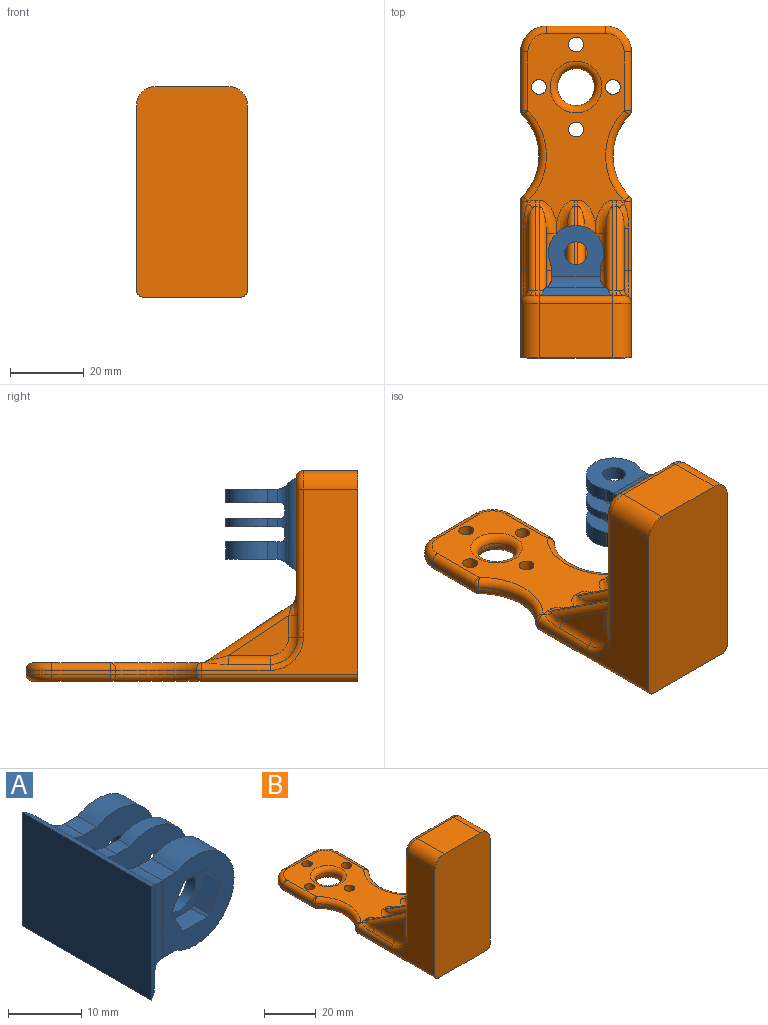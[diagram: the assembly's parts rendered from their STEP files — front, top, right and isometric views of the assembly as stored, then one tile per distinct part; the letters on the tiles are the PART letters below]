
ASSEMBLY  parts=2 mates=1
PART A: 42 faces, bbox 19x25x19 mm
  f0: plane 15x13.87mm, normal (0,-1,0), area 116.1mm2, adj f2,f6,f11,f16,f17,f18,f21,f29
  f1: cylinder r=3.7mm len=21.8mm, axis (0,-1,0), area 48.8mm2, adj f2,f3,f9,f12,f13,f14,f15,f21
  f2: plane 4.75x2.63mm, normal (0,0,-1), area 12.5mm2, adj f0,f1,f6,f27
  f3: plane 2.63x2.3mm, normal (0,0,-1), area 6mm2, adj f1,f10,f15,f28
  f4: plane 3.75x2.63mm, normal (0,0,1), area 9.8mm2, adj f7,f13,f19,f22
  f5: plane 2.63x2.3mm, normal (0,0,1), area 6mm2, adj f10,f15,f22,f28
  f6: cylinder r=7.5mm len=15mm, axis (0,1,0), area 149.1mm2, adj f0,f2,f11,f27
  f7: cylinder r=7.5mm len=15mm, axis (0,1,0), area 117.7mm2, adj f4,f9,f13,f19
  f8: plane 9.67x8.25mm, normal (0,-1,0), area 29.9mm2, adj f16,f17,f18,f26,f29,f30,f31,f32
  f9: plane 3.75x2.63mm, normal (0,0,-1), area 9.8mm2, adj f1,f7,f13,f19
  f10: cylinder r=7.5mm len=15mm, axis (0,1,0), area 72.2mm2, adj f3,f5,f15,f28
  f11: plane 4.75x2.63mm, normal (0,0,1), area 12.5mm2, adj f0,f6,f22,f27
  f12: plane 14.35x2.1mm, normal (1,0,0), area 30.1mm2, adj f1,f22,f38,f40
  f13: plane 15x15mm, normal (0,-1,0), area 160.9mm2, adj f1,f4,f7,f9,f22,f24,f40
  f14: plane 14.35x2.1mm, normal (1,0,0), area 30.1mm2, adj f1,f22,f39,f41
  f15: plane 15x15mm, normal (0,-1,0), area 160.9mm2, adj f1,f3,f5,f10,f22,f25,f41
  f16: plane 4.62x3mm, normal (0,0,1), area 13.9mm2, adj f0,f8,f18,f29
  f17: plane 4x3mm, normal (0.87,0,-0.5), area 13.9mm2, adj f0,f8,f18,f32
  f18: plane 4x3mm, normal (0.87,0,0.5), area 13.9mm2, adj f0,f8,f16,f17
  f19: plane 15x13.87mm, normal (0,1,0), area 146mm2, adj f4,f7,f9,f23,f24
  f20: plane 25x19mm, normal (-1,0,0), area 475mm2, adj f34,f35,f36,f37
  f21: cylinder r=3.7mm len=15.8mm, axis (0,0,1), area 46.5mm2, adj f0,f1,f22,f35
  f22: cylinder r=3.7mm len=21.8mm, axis (0,-1,0), area 48.8mm2, adj f4,f5,f11,f12,f13,f14,f15,f21
  f23: cylinder r=3.7mm len=15.8mm, axis (0,0,1), area 46.5mm2, adj f1,f19,f22,f36
  f24: cylinder r=3.1mm len=6.2mm, axis (0,-1,0), area 73mm2, adj f13,f19
  f25: cylinder r=3.1mm len=6.2mm, axis (0,-1,0), area 44.8mm2, adj f15,f28
  f26: cylinder r=3.1mm len=6.2mm, axis (0,-1,0), area 34.1mm2, adj f8,f27
  f27: plane 15x15mm, normal (0,1,0), area 160.9mm2, adj f1,f2,f6,f11,f22,f26,f39
  f28: plane 15x15mm, normal (0,1,0), area 160.9mm2, adj f1,f3,f5,f10,f22,f25,f38
  f29: plane 3x0.43mm, normal (-0.5,0,0.87), area 1.5mm2, adj f0,f8,f16,f30
  f30: plane 4x3mm, normal (-0.87,0,0.5), area 13.9mm2, adj f0,f8,f29,f31
  f31: plane 4x3mm, normal (-0.87,0,-0.5), area 13.9mm2, adj f0,f8,f30,f33
  f32: plane 3x0.43mm, normal (0.5,0,-0.87), area 1.5mm2, adj f0,f8,f17,f33
  f33: plane 4.62x3mm, normal (0,0,-1), area 13.9mm2, adj f0,f8,f31,f32
  f34: cylinder r=5mm len=25mm, axis (0,1,0), area 65.7mm2, adj f20,f22,f35,f36
  f35: cylinder r=5mm len=19mm, axis (0,0,-1), area 49mm2, adj f20,f21,f34,f37
  f36: cylinder r=5mm len=19mm, axis (0,0,-1), area 49mm2, adj f20,f23,f34,f37
  f37: cylinder r=5mm len=25mm, axis (0,1,0), area 65.7mm2, adj f1,f20,f35,f36
  f38: cylinder r=1mm len=14.35mm, axis (0,0,-1), area 21.9mm2, adj f1,f12,f22,f28
  f39: cylinder r=1mm len=14.35mm, axis (0,0,-1), area 21.9mm2, adj f1,f14,f22,f27
  f40: cylinder r=1mm len=14.35mm, axis (0,0,-1), area 21.9mm2, adj f1,f12,f13,f22
  f41: cylinder r=1mm len=14.35mm, axis (0,0,-1), area 21.9mm2, adj f1,f14,f15,f22
PART B: 121 faces, bbox 32.5x90.9x57.9 mm
  f0: plane 35.95x26mm, normal (0,1,0), area 845.2mm2, adj f27,f28,f29,f66,f68,f70,f72,f75
  f1: plane 16.36x10.84mm, normal (-1,0,0), area 83.3mm2, adj f63,f67,f69,f71
  f2: plane 16.36x10.84mm, normal (1,0,0), area 83.3mm2, adj f64,f90,f94,f98
  f3: plane 51.85x26.53mm, normal (0,0,1), area 821.4mm2, adj f14,f15,f16,f17,f32,f33,f34,f35
  f4: plane 21.5x14.5mm, normal (-1,0,0), area 171.8mm2, adj f6,f7,f10,f23,f24
  f5: plane 21.5x14.5mm, normal (1,0,0), area 171.8mm2, adj f6,f7,f10,f23,f24
  f6: plane 21.5x7.5mm, normal (0,0,-1), area 161.3mm2, adj f4,f5,f7,f23
  f7: plane 21.5x14.5mm, normal (0,-1,0), area 311.7mm2, adj f4,f5,f6,f24
  f8: plane 15.86x1mm, normal (1,0,0), area 15.9mm2, adj f25,f36,f45,f109
  f9: plane 15.86x1mm, normal (-1,0,0), area 15.9mm2, adj f26,f37,f46,f106
  f10: plane 87.75x26mm, normal (0,0,-1), area 1586mm2, adj f4,f5,f14,f15,f16,f17,f22,f23
  f11: plane 50x42.36mm, normal (1,0,0), area 782.5mm2, adj f22,f28,f30,f32,f41,f112,f117
  f12: plane 16x1mm, normal (0,1,0), area 16mm2, adj f25,f26,f40,f49
  f13: cylinder r=5mm len=10mm, axis (0,0,-1), area 31.4mm2, adj f50,f51
  f14: cylinder r=2mm len=5mm, axis (0,0,-1), area 62.8mm2, adj f3,f10
  f15: cylinder r=2mm len=5mm, axis (0,0,-1), area 62.8mm2, adj f3,f10
  f16: cylinder r=2mm len=5mm, axis (0,0,-1), area 62.8mm2, adj f3,f10
  f17: cylinder r=2mm len=5mm, axis (0,0,-1), area 62.8mm2, adj f3,f10
  f18: plane 50x42.36mm, normal (-1,0,0), area 782.5mm2, adj f22,f29,f31,f33,f42,f115,f119
  f19: cylinder r=15.54mm len=21.73mm, axis (0,0,1), area 24.1mm2, adj f34,f43,f109,f112
  f20: cylinder r=15.54mm len=21.73mm, axis (0,0,1), area 24.1mm2, adj f35,f44,f106,f115
  f21: plane 20x14.75mm, normal (0,0,1), area 295mm2, adj f22,f27,f117,f119
  f22: plane 57x30mm, normal (0,-1,0), area 1697.6mm2, adj f10,f11,f18,f21,f41,f42,f117,f119
  f23: plane 21.5x21.5mm, normal (0,1,0), area 462.2mm2, adj f4,f5,f6,f10
  f24: cylinder r=7mm len=21.5mm, axis (1,0,0), area 236.4mm2, adj f4,f5,f7,f10
  f25: cylinder r=7mm len=7mm, axis (0,0,-1), area 11mm2, adj f8,f12,f38,f47
  f26: cylinder r=7mm len=7mm, axis (0,0,1), area 11mm2, adj f9,f12,f39,f48
  f27: cylinder r=2mm len=20mm, axis (1,0,0), area 62.8mm2, adj f0,f21,f118,f120
  f28: cylinder r=2mm len=40mm, axis (0,0,1), area 115mm2, adj f0,f11,f30,f85,f90,f118
  f29: cylinder r=2mm len=40mm, axis (0,0,-1), area 115mm2, adj f0,f18,f31,f65,f67,f120
  f30: torus R=9mm, axis (-1,0,0), area 23.7mm2, adj f11,f28,f32,f94
  f31: torus R=9mm, axis (-1,0,0), area 23.7mm2, adj f18,f29,f33,f69
  f32: cylinder r=2mm len=18.61mm, axis (0,-1,0), area 37.6mm2, adj f3,f11,f30,f98,f101,f111
  f33: cylinder r=2mm len=18.61mm, axis (0,1,0), area 37.6mm2, adj f3,f18,f31,f71,f74,f114
  f34: torus R=17.54mm, axis (0,0,1), area 79.1mm2, adj f3,f19,f108,f111
  f35: torus R=17.54mm, axis (0,0,1), area 79.1mm2, adj f3,f20,f105,f114
  f36: cylinder r=2mm len=15.86mm, axis (0,-1,0), area 49.8mm2, adj f3,f8,f38,f108
  f37: cylinder r=2mm len=15.86mm, axis (0,1,0), area 49.8mm2, adj f3,f9,f39,f105
  f38: torus R=5mm, axis (0,0,1), area 31mm2, adj f3,f25,f36,f40
  f39: torus R=5mm, axis (0,0,1), area 31mm2, adj f3,f26,f37,f40
  f40: cylinder r=2mm len=16mm, axis (1,0,0), area 50.3mm2, adj f3,f12,f38,f39
  f41: cylinder r=2mm len=42.36mm, axis (0,1,0), area 133.1mm2, adj f10,f11,f22,f113
  f42: cylinder r=2mm len=42.36mm, axis (0,-1,0), area 133.1mm2, adj f10,f18,f22,f116
  f43: torus R=17.54mm, axis (0,0,1), area 79.1mm2, adj f10,f19,f110,f113
  f44: torus R=17.54mm, axis (0,0,1), area 79.1mm2, adj f10,f20,f107,f116
  f45: cylinder r=2mm len=15.86mm, axis (0,1,0), area 49.8mm2, adj f8,f10,f47,f110
  f46: cylinder r=2mm len=15.86mm, axis (0,-1,0), area 49.8mm2, adj f9,f10,f48,f107
  f47: torus R=5mm, axis (0,0,1), area 31mm2, adj f10,f25,f45,f49
  f48: torus R=5mm, axis (0,0,1), area 31mm2, adj f10,f26,f46,f49
  f49: cylinder r=2mm len=16mm, axis (-1,0,0), area 50.3mm2, adj f10,f12,f47,f48
  f50: torus R=7mm, axis (0,0,1), area 113mm2, adj f10,f13
  f51: torus R=7mm, axis (0,0,1), area 113mm2, adj f3,f13
  f52: plane 13.85x9.18mm, normal (1,0,0), area 60.1mm2, adj f59,f73,f77,f83
  f53: plane 13.85x9.18mm, normal (-1,0,0), area 60.1mm2, adj f60,f76,f82,f88
  f54: plane 13.85x9.18mm, normal (1,0,0), area 60.1mm2, adj f61,f87,f92,f96
  f55: plane 13.85x9.18mm, normal (-1,0,0), area 60.1mm2, adj f62,f91,f95,f99
  f56: plane 22.9x15.18mm, normal (0,0.55,0.83), area 27.5mm2, adj f62,f64,f80,f104
  f57: plane 22.9x15.18mm, normal (0,0.55,0.83), area 27.5mm2, adj f60,f61,f75,f97
  f58: plane 22.9x15.18mm, normal (0,0.55,0.83), area 27.5mm2, adj f59,f63,f68,f84
  f59: cylinder r=2mm len=24.01mm, axis (0,-0.83,0.55), area 69.3mm2, adj f52,f58,f70,f89
  f60: cylinder r=2mm len=24.01mm, axis (0,0.83,-0.55), area 69.3mm2, adj f53,f57,f72,f93
  f61: cylinder r=2mm len=24.01mm, axis (0,-0.83,0.55), area 69.3mm2, adj f54,f57,f81,f100
  f62: cylinder r=2mm len=24.01mm, axis (0,0.83,-0.55), area 69.3mm2, adj f55,f56,f86,f102
  f63: cylinder r=2mm len=24.01mm, axis (0,-0.83,0.55), area 75.8mm2, adj f1,f58,f65,f66,f74,f78
  f64: cylinder r=2mm len=24.01mm, axis (0,0.83,-0.55), area 75.8mm2, adj f2,f56,f79,f85,f101,f103
  f65: bspline ~5.65x2.62mm, area 9.9mm2, adj f29,f63,f66,f67
  f66: bspline ~2.79x2mm, area 4.3mm2, adj f0,f63,f65,f68
  f67: cylinder r=3mm len=5.84mm, axis (0,0,-1), area 16.2mm2, adj f1,f29,f65,f69
  f68: cylinder r=3mm len=2.5mm, axis (1,0,0), area 3mm2, adj f0,f58,f66,f70
  f69: torus R=5mm, axis (-1,0,0), area 27.5mm2, adj f1,f31,f67,f71
  f70: bspline ~6x5mm, area 22.5mm2, adj f0,f59,f68,f72,f73
  f71: cylinder r=3mm len=11.36mm, axis (0,1,0), area 31.6mm2, adj f1,f33,f69,f74
  f72: bspline ~6x5mm, area 22.5mm2, adj f0,f60,f70,f75,f76
  f73: cylinder r=3mm len=5.18mm, axis (0,0,-1), area 23.1mm2, adj f52,f70,f76,f77
  f74: bspline ~9.27x3.03mm, area 13.1mm2, adj f33,f63,f71,f78
  f75: cylinder r=3mm len=2.5mm, axis (1,0,0), area 3mm2, adj f0,f57,f72,f81
  f76: cylinder r=3mm len=5.18mm, axis (0,0,1), area 23.1mm2, adj f53,f72,f73,f82
  f77: torus R=4mm, axis (-1,0,0), area 41mm2, adj f52,f73,f82,f83
  f78: bspline ~2.27x2mm, area 3mm2, adj f3,f63,f74,f84
  f79: bspline ~2.79x2mm, area 4.3mm2, adj f0,f64,f80,f85
  f80: cylinder r=3mm len=2.5mm, axis (1,0,0), area 3mm2, adj f0,f56,f79,f86
  f81: bspline ~7.04x5mm, area 22.5mm2, adj f0,f61,f75,f86,f87
  f82: torus R=4mm, axis (-1,0,0), area 41mm2, adj f53,f76,f77,f88
  f83: cylinder r=3mm len=9.85mm, axis (0,1,0), area 44mm2, adj f52,f77,f88,f89
  f84: cylinder r=3mm len=1.66mm, axis (1,0,0), area 1.8mm2, adj f3,f58,f78,f89
  f85: bspline ~5.65x2.62mm, area 9.9mm2, adj f28,f64,f79,f90
  f86: bspline ~6x5mm, area 22.5mm2, adj f0,f62,f80,f81,f91
  f87: cylinder r=3mm len=5.18mm, axis (0,0,-1), area 23.1mm2, adj f54,f81,f91,f92
  f88: cylinder r=3mm len=9.85mm, axis (0,-1,0), area 44mm2, adj f53,f82,f83,f93
  f89: bspline ~9.05x5mm, area 29.6mm2, adj f3,f59,f83,f84,f93
  f90: cylinder r=3mm len=5.84mm, axis (0,0,1), area 16.2mm2, adj f2,f28,f85,f94
  f91: cylinder r=3mm len=5.18mm, axis (0,0,1), area 23.1mm2, adj f55,f86,f87,f95
  f92: torus R=4mm, axis (-1,0,0), area 41mm2, adj f54,f87,f95,f96
  f93: bspline ~9.05x5mm, area 29.6mm2, adj f3,f60,f88,f89,f97
  f94: torus R=5mm, axis (1,0,0), area 27.5mm2, adj f2,f30,f90,f98
  f95: torus R=4mm, axis (-1,0,0), area 41mm2, adj f55,f91,f92,f99
  f96: cylinder r=3mm len=9.85mm, axis (0,1,0), area 44mm2, adj f54,f92,f99,f100
  f97: cylinder r=3mm len=1.66mm, axis (1,0,0), area 1.8mm2, adj f3,f57,f93,f100
  f98: cylinder r=3mm len=11.36mm, axis (0,-1,0), area 31.6mm2, adj f2,f32,f94,f101
  f99: cylinder r=3mm len=9.85mm, axis (0,-1,0), area 44mm2, adj f55,f95,f96,f102
  f100: bspline ~9.05x5mm, area 29.6mm2, adj f3,f61,f96,f97,f102
  f101: bspline ~9.27x3.03mm, area 13.1mm2, adj f32,f64,f98,f103
  f102: bspline ~9.05x5mm, area 29.6mm2, adj f3,f62,f99,f100,f104
  f103: bspline ~2.27x2mm, area 3mm2, adj f3,f64,f101,f104
  f104: cylinder r=3mm len=1.66mm, axis (1,0,0), area 1.8mm2, adj f3,f56,f102,f103
  f105: sphere r=2mm, area 3.1mm2, adj f35,f37,f106
  f106: cylinder r=2mm len=1.4mm, axis (0,0,1), area 1.5mm2, adj f9,f20,f105,f107
  f107: sphere r=2mm, area 3.1mm2, adj f44,f46,f106
  f108: sphere r=2mm, area 3.1mm2, adj f34,f36,f109
  f109: cylinder r=2mm len=1.4mm, axis (0,0,1), area 1.5mm2, adj f8,f19,f108,f110
  f110: sphere r=2mm, area 3.1mm2, adj f43,f45,f109
  f111: sphere r=2mm, area 2mm2, adj f32,f34,f112
  f112: cylinder r=2mm len=1.4mm, axis (0,0,1), area 1.5mm2, adj f11,f19,f111,f113
  f113: sphere r=2mm, area 2mm2, adj f41,f43,f112
  f114: sphere r=2mm, area 3.1mm2, adj f33,f35,f115
  f115: cylinder r=2mm len=1.4mm, axis (0,0,1), area 1.5mm2, adj f18,f20,f114,f116
  f116: sphere r=2mm, area 3.1mm2, adj f42,f44,f115
  f117: cylinder r=5mm len=14.75mm, axis (0,-1,0), area 115.8mm2, adj f11,f21,f22,f118
  f118: torus R=3mm, axis (0,1,0), area 21.1mm2, adj f0,f27,f28,f117
  f119: cylinder r=5mm len=14.75mm, axis (0,1,0), area 115.8mm2, adj f18,f21,f22,f120
  f120: torus R=3mm, axis (0,1,0), area 21.1mm2, adj f0,f27,f29,f119
PLACE A rot(axis=(0.58,0.58,0.58),120deg) t=(-15.15,-18.2,27.91)mm
PLACE B t=(-15.15,29.8,-15.59)mm
MATE fastened A.f20 <-> B.f0  axis (0,-1,0) through (-15.15,-26.7,39.41)mm
